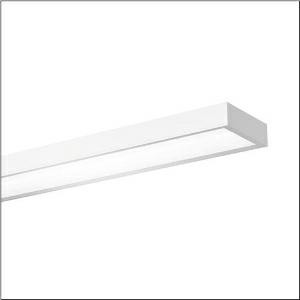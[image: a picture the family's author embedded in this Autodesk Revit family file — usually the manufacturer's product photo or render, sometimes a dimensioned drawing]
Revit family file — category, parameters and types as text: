
# Revit family: sport_31_51hs12dc4dca
name_source: partatom
category: Lighting Fixtures
units: mm (PartAtom-declared; Revit-internal decimal feet)

## family parameters
Cut with Voids When Loaded = No
Host = Face
Light Source = No
Part Type = Normal
Room Calculation Point = No
Round Connector Dimension = Use Diameter
Shared = No

## types (1)
- --- (1 x LED, 8000 lm, 59.4 W, 4000K)
    Apparent Load = 59 VA
    CIE Flux Codes = 65 89 97 100 100
    Color Rendering = 80
    Color Temperature = 4000K
    Default Elevation = 1800 mm
    Description = Sport 31, LED high bay luminaire, primary light control with reflector, of sheet steel, primary anti-glare with prismatic structure, of PC, primary optical cover: cover panel, of PC, light emission: direct distribution, primary light characteristic: symmetric, installation type: suspended mounting, recessed, surface-mounted, LED, rated luminous flux: 8.000lm, luminous efficacy: 135lm/W, light colour: 840, colour temperature: 4000K, control gear: DALI 2, with terminal, 5-pole, max. 2.5mm², mains connection: 220..240V, AC/DC, 50/60Hz, rated input power: 58W, housing, of sheet steel, traffic white (RAL 9016), length: 1.540mm, width: 315mm, height: 95mm, protection rating (complete): IP20, protection rating (lamp compartment, on room side): IP50, insulation class (complete): insulation class I (protective earthing), certification: CE, ENEC, UKCA, ball protection: ball impact resistant with ceiling mounting or chain suspension, impact resistance: IK08, permissible operating ambient temperature: -20..+35°C, standard: DIN 18032-3, EN 60598-2-22, packaging unit: 1 piece
    Height = 100 mm  [stored 0.328084 ft]
    Lamp = 1 x LED
    Lamp Light Flux = 8000 lm
    Lamp Power = 59.4 W
    Lamp count = 1
    Length = 1500 mm
    Luminous efficacy = 135 lm/W
    Manufacturer = Siteco
    ModVariant = No
    Model = 51HS12DC4DCA
    Mounting Place = Ceiling
    Mounting Type = Pendant
    Number of Poles = 1
    OnlyDefault = Yes
    Power Factor = 1
    Product Name = Sport 31
    Product group = LED high bay luminaire
    ProductGroupID = 903
    Protection Class = Protection class I
    Protection Degree = IP 20
    RLX_Detail_Level = 1
    RLX_Emergency_Light_Flux = 0 lm
    RLX_Emergency_Type = 0
    RLX_Emergency_Type_DB = No
    RlxData = <blob elided: 22797 chars, md5=80204926>
    Socket = socket
    Standby Power = 0 W
    System Light Flux = 8000 lm
    System Power = 59 W
    Type Comments = factory setting: luminous flux: 100 % | dim-lin: 254 | 247 mA
    Type Image = l_1006823.jpg
    URL = http://relux.com
    VarID = @adj_197218
    Voltage = 0 V
    Weight = 0.00 kg
    Width = 315 mm

note: [stored X ft] marks values corroborated as IEEE doubles in the binary element streams (Revit-internal decimal feet)

## geometry (parser evidence)
native form markers: Blend x4, Sweep x9
no freeform markers — native parametric forms only
